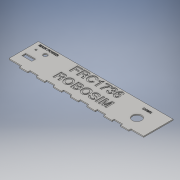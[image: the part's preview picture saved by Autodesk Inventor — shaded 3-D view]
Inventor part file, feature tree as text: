
AUTODESK INVENTOR PART (.ipt)
format: ipt  version: 2016 (Build 200138000, 138)  size: 701,440 bytes
history: native  units: in
note: dims shown in document units (in); Inventor stores cm internally (conversion verified against a paired STEP export)
features: extrude x8, sketch x8
ambient origin geometry x8: Origin, YZ Plane, XZ Plane, XY Plane, X Axis, Y Axis, Z Axis, Center Point
bodies: Solid1 (feature_tree)
feature tree (16):
  extrude  "Extrusion1"  Depth=3.5in
  extrude  "Extrusion2"  Depth=1.0in
  sketch  "Sketch1"  dims[d0=16.0in d1=3.5in]
  sketch  "Sketch2"  dims[d2=0.125in d3=0.0in d4=2.7559in d6=2.0in d7=0.3937in d9=1.0in]
  sketch  "Sketch4"  dims[d17=0.1969in d19=0.0in d20=0.075in]
  sketch  "Sketch7"  dims[d36=0.0in d37=0.075in]
  sketch  "Sketch8"
  extrude  "Extrusion3"  Depth=1.1in TaperAngle=0.0deg
  extrude  "Extrusion4"  Depth=0.075in TaperAngle=0.0deg
  extrude  "Extrusion5"  Depth=0.1969in
  extrude  "Extrusion6"  Depth=0.075in TaperAngle=0.0deg
  extrude  "Extrusion7"  [1 undecoded]
  extrude  "Extrusion8"  [1 undecoded]
  sketch  "Sketch3"  dims[d11=0.125in d12=0.0in d13=1.1in d15=0.0in d16=0.1969in]
  sketch  "Sketch5"  dims[d21=1.1811in d22=0.4528in d24=0.0in d25=0.1969in d26=0.1969in]
  sketch  "Sketch6"  dims[d27=0.4724in d28=0.1969in d30=0.0in d31=0.1969in d33=0.0in d34=0.075in]
note: 2 required parameter values undecoded (feature->parameter linkage not recoverable at this tier; creation-order binding heuristic only, values carry confidence <= 0.55)
